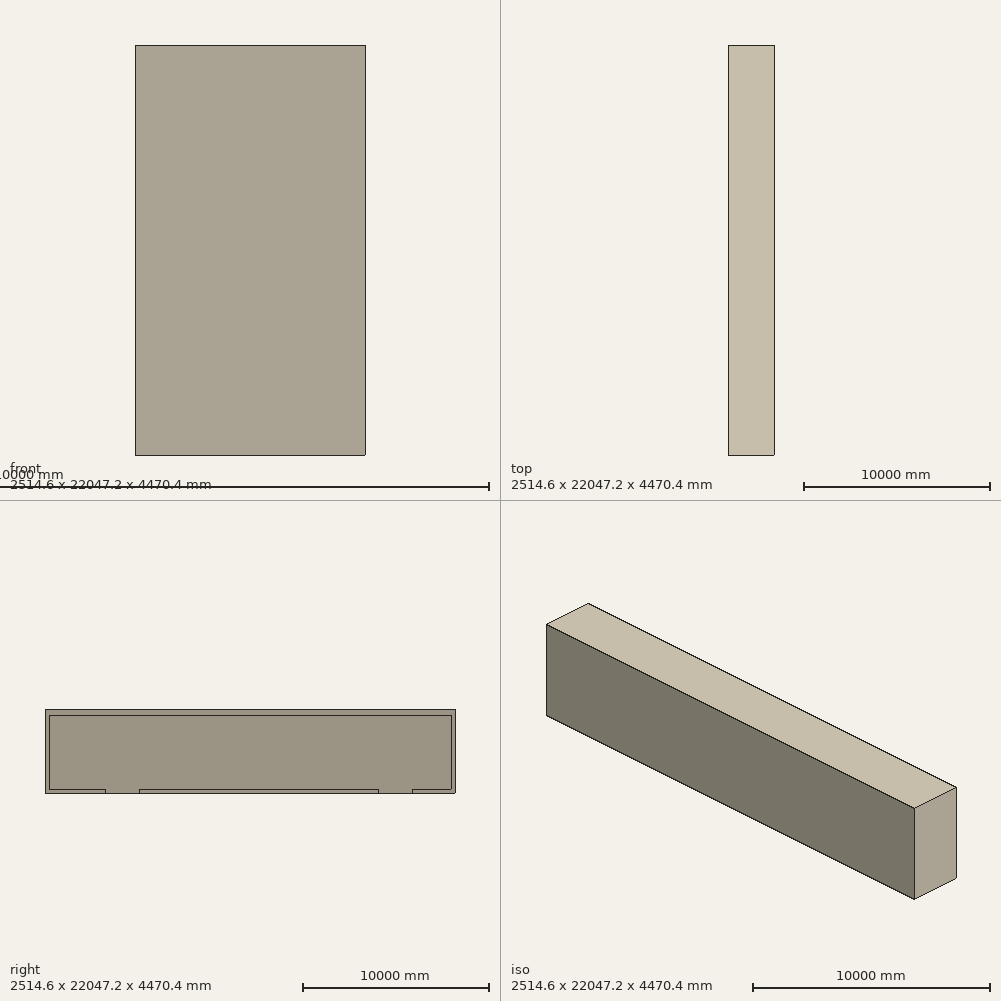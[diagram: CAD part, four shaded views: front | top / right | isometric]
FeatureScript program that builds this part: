
annotation { "Feature Type Name" : "Feature", "Feature Type Description" : "" }
export const myFeature = defineFeature(function(context is Context, id is Id, definition is map)
    precondition{}
    {
        {
            var Q0;
            Q0=qCreatedBy(makeId("Right.planeOp"),FACE);
            var sketch = newSketch(context, id + "F0", { "sketchPlane" : qUnion([Q0])});
            skLineSegment(sketch, "E0.bottom", {"start": v(0, 0) * mm, "end": v(-2133.6, 0) * mm});
            skLineSegment(sketch, "E0.top", {"start": v(0, 3962.4) * mm, "end": v(-21640.8, 3962.4) * mm});
            skLineSegment(sketch, "E0.left", {"start": v(0, 0) * mm, "end": v(0, 3962.4) * mm});
            skLineSegment(sketch, "E0.right", {"start": v(-21640.8, 0) * mm, "end": v(-21640.8, 3962.4) * mm});
            skLineSegment(sketch, "E1.bottom", {"start": v(-21844, 4267.2) * mm, "end": v(203.2, 4267.2) * mm});
            skLineSegment(sketch, "E1.top", {"start": v(-21844, -203.2) * mm, "end": v(-18592.8, -203.2) * mm});
            skLineSegment(sketch, "E1.left", {"start": v(-21844, 4267.2) * mm, "end": v(-21844, -203.2) * mm});
            skLineSegment(sketch, "E1.right", {"start": v(203.2, 4267.2) * mm, "end": v(203.2, -203.2) * mm});
            skLineSegment(sketch, "E2.left", {"start": v(-18592.8, 0) * mm, "end": v(-18592.8, -203.2) * mm});
            skLineSegment(sketch, "E2.right", {"start": v(-16764, 0) * mm, "end": v(-16764, -203.2) * mm});
            skLineSegment(sketch, "E3.left", {"start": v(-2133.6, 0) * mm, "end": v(-2133.6, -203.2) * mm});
            skLineSegment(sketch, "E3.right", {"start": v(-3962.4, 0) * mm, "end": v(-3962.4, -203.2) * mm});
            skLineSegment(sketch, "E4.trimOffspring", {"start": v(-18592.8, 0) * mm, "end": v(-21640.8, 0) * mm});
            skLineSegment(sketch, "E5.trimOffspring", {"start": v(-16764, -203.2) * mm, "end": v(-3962.4, -203.2) * mm});
            skLineSegment(sketch, "E6.trimOffspring", {"start": v(-2133.6, -203.2) * mm, "end": v(203.2, -203.2) * mm});
            skLineSegment(sketch, "E7.trimOffspring", {"start": v(-3962.4, 0) * mm, "end": v(-16764, 0) * mm});
            skSolve(sketch);
        }
        {
            var Q0;
            Q0 = qSketchRegion(id + "F0", true);
            extrude(context, id + "F1", {"entities" : qUnion([Q0]), "depth" : 2438.4 * mm});
        }
        {
            var Q0;
            Q0=makeQuery(id+"F1.opExtrude","CAP_FACE",FACE,{"disambiguationData":[OSD([sQuery(id+"F0.wireOp",EDGE,"E0.bottom"),sQuery(id+"F0.wireOp",EDGE,"E0.top"),sQuery(id+"F0.wireOp",EDGE,"E0.left"),sQuery(id+"F0.wireOp",EDGE,"E0.right"),sQuery(id+"F0.wireOp",EDGE,"E1.bottom"),sQuery(id+"F0.wireOp",EDGE,"E1.top"),sQuery(id+"F0.wireOp",EDGE,"E1.left"),sQuery(id+"F0.wireOp",EDGE,"E1.right"),sQuery(id+"F0.wireOp",EDGE,"E2.left"),sQuery(id+"F0.wireOp",EDGE,"E3.left"),sQuery(id+"F0.wireOp",EDGE,"E4.trimOffspring"),sQuery(id+"F0.wireOp",EDGE,"E6.trimOffspring")])],"isStart":true});
            var sketch = newSketch(context, id + "F2", { "sketchPlane" : qUnion([Q0])});
            skLineSegment(sketch, "E8.bottom", {"start": v(-203.2, -203.2) * mm, "end": v(21844, -203.2) * mm});
            skLineSegment(sketch, "E8.top", {"start": v(-203.2, 4267.2) * mm, "end": v(21844, 4267.2) * mm});
            skLineSegment(sketch, "E8.left", {"start": v(-203.2, -203.2) * mm, "end": v(-203.2, 4267.2) * mm});
            skLineSegment(sketch, "E8.right", {"start": v(21844, -203.2) * mm, "end": v(21844, 4267.2) * mm});
            skSolve(sketch);
        }
        {
            var Q0;
            Q0 = qSketchRegion(id + "F2", true);
            extrude(context, id + "F3", {"entities" : qUnion([Q0]), "operationType" : NewBodyOperationType.ADD, "depth" : 76.2 * mm});
        }
    });
